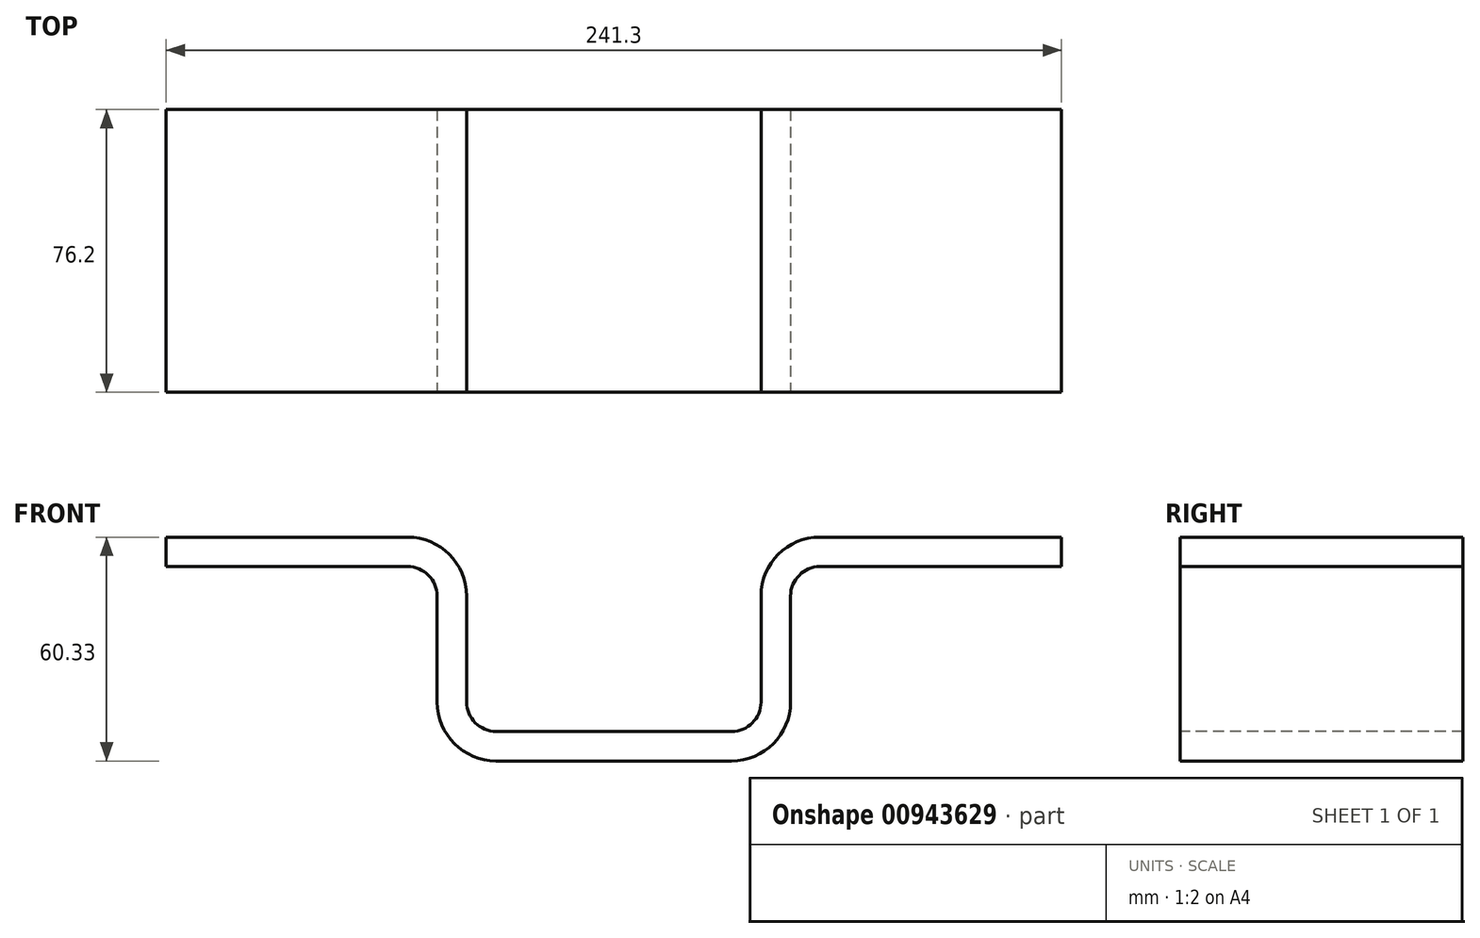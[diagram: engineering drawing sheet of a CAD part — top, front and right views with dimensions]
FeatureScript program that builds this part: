
annotation { "Feature Type Name" : "Feature", "Feature Type Description" : "" }
export const myFeature = defineFeature(function(context is Context, id is Id, definition is map)
    precondition{}
    {
        {
            var Q0;
            Q0=qCreatedBy(makeId("Top.planeOp"),FACE);
            var sketch = newSketch(context, id + "F0", { "sketchPlane" : qUnion([Q0])});
            skLineSegment(sketch, "E0.bottom", {"start": v(0, 0) * mm, "end": v(241.3, 0) * mm});
            skLineSegment(sketch, "E0.top", {"start": v(0, 76.2) * mm, "end": v(241.3, 76.2) * mm});
            skLineSegment(sketch, "E0.left", {"start": v(0, 0) * mm, "end": v(0, 76.2) * mm});
            skLineSegment(sketch, "E0.right", {"start": v(241.3, 0) * mm, "end": v(241.3, 76.2) * mm});
            skSolve(sketch);
        }
        {
            var Q0;
            Q0 = qSketchRegion(id + "F0", true);
            extrude(context, id + "F1", {"entities" : qUnion([Q0]), "depth" : 60.32 * mm, "offsetDistance" : 25.4 * mm});
        }
        {
            var Q0;
            Q0=qCreatedBy(makeId("Front.planeOp"),FACE);
            var sketch = newSketch(context, id + "F2", { "sketchPlane" : qUnion([Q0])});
            skLineSegment(sketch, "E1.top", {"start": v(0, 52.37) * mm, "end": v(65.07, 52.37) * mm});
            skLineSegment(sketch, "E1.left", {"start": v(0, 0) * mm, "end": v(0, 52.37) * mm});
            skLineSegment(sketch, "E1.right", {"start": v(73.03, 15.87) * mm, "end": v(73.03, 44.42) * mm});
            skLineSegment(sketch, "E2.top", {"start": v(241.3, 52.37) * mm, "end": v(176.23, 52.37) * mm});
            skLineSegment(sketch, "E2.left", {"start": v(241.3, 0) * mm, "end": v(241.3, 52.37) * mm});
            skLineSegment(sketch, "E2.right", {"start": v(168.28, 15.87) * mm, "end": v(168.28, 44.42) * mm});
            skLineSegment(sketch, "E3.top", {"start": v(88.93, 7.95) * mm, "end": v(152.44, 7.95) * mm});
            skLineSegment(sketch, "E3.left", {"start": v(80.98, 44.45) * mm, "end": v(80.98, 15.9) * mm});
            skLineSegment(sketch, "E3.right", {"start": v(160.32, 44.45) * mm, "end": v(160.32, 15.83) * mm});
            skLineSegment(sketch, "E4", {"start": v(65.1, 60.33) * mm, "end": v(0, 60.33) * mm});
            skLineSegment(sketch, "E5", {"start": v(0, 60.33) * mm, "end": v(0, 52.37) * mm});
            skLineSegment(sketch, "E6", {"start": v(176.2, 60.33) * mm, "end": v(241.3, 60.33) * mm});
            skLineSegment(sketch, "E7", {"start": v(241.3, 60.33) * mm, "end": v(241.3, 52.37) * mm});
            skLineSegment(sketch, "E8", {"start": v(88.9, 0) * mm, "end": v(152.4, 0) * mm});
            skPoint(sketch, "E9.visualSharp", {"position": v(80.98, 60.33) * mm});
            skArc(sketch, "E9.filletArc", {"start": v(80.98, 44.45) * mm, "mid": v(76.33, 55.68) * mm, "end": v(65.1, 60.33) * mm});
            skPoint(sketch, "E10.visualSharp", {"position": v(160.32, 60.33) * mm});
            skArc(sketch, "E10.filletArc", {"start": v(176.2, 60.33) * mm, "mid": v(164.97, 55.68) * mm, "end": v(160.32, 44.45) * mm});
            skPoint(sketch, "E11.visualSharp", {"position": v(168.28, 0) * mm});
            skArc(sketch, "E11.filletArc", {"start": v(152.4, 0) * mm, "mid": v(163.63, 4.65) * mm, "end": v(168.28, 15.87) * mm});
            skPoint(sketch, "E12.visualSharp", {"position": v(73.03, 0) * mm});
            skArc(sketch, "E12.filletArc", {"start": v(73.03, 15.87) * mm, "mid": v(77.67, 4.65) * mm, "end": v(88.9, 0) * mm});
            skPoint(sketch, "E13.visualSharp", {"position": v(80.98, 7.95) * mm});
            skArc(sketch, "E13.filletArc", {"start": v(80.98, 15.9) * mm, "mid": v(83.3, 10.28) * mm, "end": v(88.93, 7.95) * mm});
            skPoint(sketch, "E14.visualSharp", {"position": v(73.03, 52.37) * mm});
            skArc(sketch, "E14.filletArc", {"start": v(73.03, 44.42) * mm, "mid": v(70.7, 50.05) * mm, "end": v(65.07, 52.37) * mm});
            skPoint(sketch, "E15.visualSharp", {"position": v(168.28, 52.37) * mm});
            skArc(sketch, "E15.filletArc", {"start": v(176.23, 52.37) * mm, "mid": v(170.6, 50.05) * mm, "end": v(168.27, 44.42) * mm});
            skPoint(sketch, "E16.visualSharp", {"position": v(160.32, 7.95) * mm});
            skArc(sketch, "E16.filletArc", {"start": v(152.44, 7.95) * mm, "mid": v(158.02, 10.26) * mm, "end": v(160.32, 15.83) * mm});
            skLineSegment(sketch, "E17", {"start": v(0, 52.37) * mm, "end": v(0, 0) * mm});
            skLineSegment(sketch, "E18", {"start": v(0, 0) * mm, "end": v(88.9, 0) * mm});
            skLineSegment(sketch, "E19", {"start": v(65.1, 60.33) * mm, "end": v(176.2, 60.33) * mm});
            skLineSegment(sketch, "E20", {"start": v(152.4, 0) * mm, "end": v(241.3, 0) * mm});
            skLineSegment(sketch, "E21", {"start": v(241.3, 52.37) * mm, "end": v(241.3, 0) * mm});
            skSolve(sketch);
        }
        {
            var Q0;
            Q0=makeQuery(id+"F2.imprint","IMPRINT",FACE,{"disambiguationData":[TD([[makeQuery(id+"F2.imprint","IMPRINT",EDGE,{"derivedFrom":sQuery(id+"F2.wireOp",EDGE,"E1.top")}),-1.0]])]});
            var Q1;
            Q1=makeQuery(id+"F2.imprint","IMPRINT",FACE,{"disambiguationData":[TD([[makeQuery(id+"F2.imprint","IMPRINT",EDGE,{"derivedFrom":sQuery(id+"F2.wireOp",EDGE,"E3.top")}),1.0]])]});
            var Q2;
            Q2=makeQuery(id+"F2.imprint","IMPRINT",FACE,{"disambiguationData":[TD([[makeQuery(id+"F2.imprint","IMPRINT",EDGE,{"derivedFrom":sQuery(id+"F2.wireOp",EDGE,"E2.top")}),1.0]])]});
            extrude(context, id + "F3", {"entities" : qUnion([Q0, Q1, Q2]), "operationType" : NewBodyOperationType.REMOVE, "endBound" : BoundingType.THROUGH_ALL, "oppositeDirection" : true, "depth" : 25.4 * mm, "offsetDistance" : 25.4 * mm});
        }
    });
